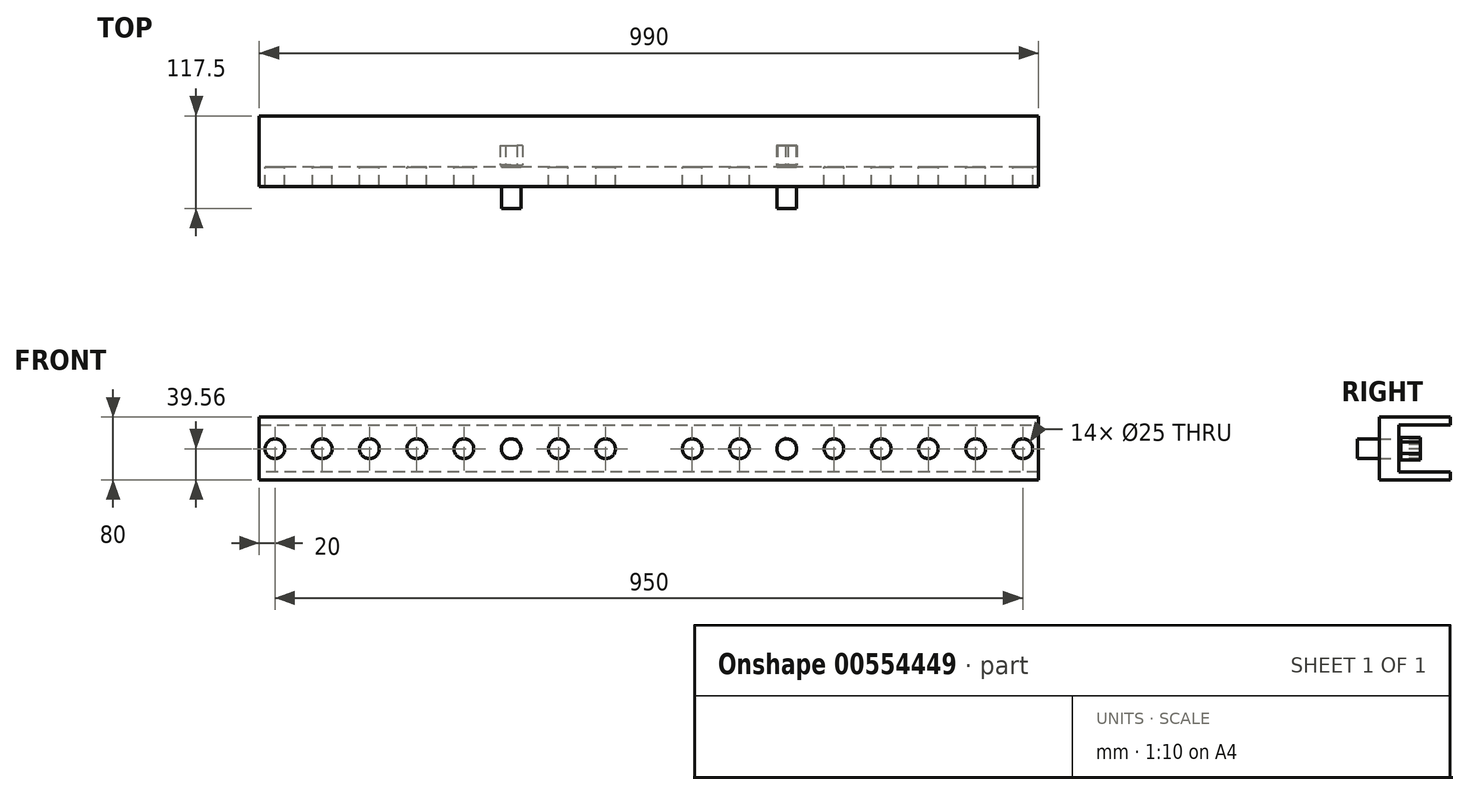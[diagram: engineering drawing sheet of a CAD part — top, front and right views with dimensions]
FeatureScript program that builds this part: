
annotation { "Feature Type Name" : "Feature", "Feature Type Description" : "" }
export const myFeature = defineFeature(function(context is Context, id is Id, definition is map)
    precondition{}
    {
        {
            var Q0;
            Q0=qCreatedBy(makeId("Front.planeOp"),FACE);
            var sketch = newSketch(context, id + "F0", { "sketchPlane" : qUnion([Q0])});
            skLineSegment(sketch, "E0.top", {"start": v(-325, -39.56) * mm, "end": v(325, -39.56) * mm});
            skLineSegment(sketch, "E0.left", {"start": v(-325, 40.44) * mm, "end": v(-325, -39.56) * mm});
            skLineSegment(sketch, "E0.right", {"start": v(325, 40.44) * mm, "end": v(325, -39.56) * mm});
            skLineSegment(sketch, "E1", {"start": v(-325, 40.44) * mm, "end": v(0, 40.44) * mm});
            skLineSegment(sketch, "E2", {"start": v(0, 40.44) * mm, "end": v(325, 40.44) * mm});
            skCircle(sketch, "E3", {"center": v(-295, 0) * mm, "radius": 12.5 * mm});
            skCircle(sketch, "E4", {"center": v(-235, 0) * mm, "radius": 12.5 * mm});
            skCircle(sketch, "E5", {"center": v(-175, 0) * mm, "radius": 12.5 * mm});
            skCircle(sketch, "E6", {"center": v(175, 0) * mm, "radius": 12.5 * mm});
            skCircle(sketch, "E7", {"center": v(235, 0) * mm, "radius": 12.5 * mm});
            skCircle(sketch, "E8", {"center": v(295, 0) * mm, "radius": 12.5 * mm});
            skLineSegment(sketch, "E9", {"start": v(325, 40.44) * mm, "end": v(495, 40.44) * mm});
            skLineSegment(sketch, "E10", {"start": v(-325, 40.44) * mm, "end": v(-495, 40.44) * mm});
            skLineSegment(sketch, "E11", {"start": v(-495, 40.44) * mm, "end": v(-495, -39.56) * mm});
            skLineSegment(sketch, "E12", {"start": v(-495, -39.56) * mm, "end": v(-325, -39.56) * mm});
            skLineSegment(sketch, "E13", {"start": v(495, 40.44) * mm, "end": v(495, -39.56) * mm});
            skLineSegment(sketch, "E14", {"start": v(495, -39.56) * mm, "end": v(325, -39.56) * mm});
            skCircle(sketch, "E15", {"center": v(355, 0) * mm, "radius": 12.5 * mm});
            skCircle(sketch, "E16", {"center": v(415, 0) * mm, "radius": 12.5 * mm});
            skCircle(sketch, "E17", {"center": v(475, 0) * mm, "radius": 12.5 * mm});
            skCircle(sketch, "E18", {"center": v(115, 0) * mm, "radius": 12.5 * mm});
            skCircle(sketch, "E19", {"center": v(55, 0) * mm, "radius": 12.5 * mm});
            skCircle(sketch, "E20", {"center": v(-55, 0) * mm, "radius": 12.5 * mm});
            skCircle(sketch, "E21", {"center": v(-115, 0) * mm, "radius": 12.5 * mm});
            skCircle(sketch, "E22", {"center": v(-355, 0) * mm, "radius": 12.5 * mm});
            skCircle(sketch, "E23", {"center": v(-415, 0) * mm, "radius": 12.5 * mm});
            skCircle(sketch, "E24", {"center": v(-475, 0) * mm, "radius": 12.5 * mm});
            skSolve(sketch);
        }
        {
            var Q0;
            Q0 = qSketchRegion(id + "F0", true);
            extrude(context, id + "F1", {"entities" : qUnion([Q0]), "depth" : 25 * mm, "offsetDistance" : 25 * mm});
        }
        {
            var Q0;
            {var subQ0=sQuery(id+"F0.wireOp",EDGE,"E8");var subQ1=sQuery(id+"F0.wireOp",EDGE,"E7");var subQ2=sQuery(id+"F0.wireOp",EDGE,"E6");var subQ3=sQuery(id+"F0.wireOp",EDGE,"E5");var subQ4=sQuery(id+"F0.wireOp",EDGE,"E4");var subQ5=sQuery(id+"F0.wireOp",EDGE,"E3");Q0=makeQuery(id+"FZENVl10s8qZQgk_7.boolean.opBoolean","MERGE",FACE,{"derivedFrom":[makeQuery(id+"Faq082uHJgfn2bv_0.opExtrude","CAP_FACE",FACE,{"disambiguationData":[OSD([subQ5])],"isStart":true}),makeQuery(id+"Faq082uHJgfn2bv_0.opExtrude","CAP_FACE",FACE,{"disambiguationData":[OSD([subQ4])],"isStart":true}),makeQuery(id+"Faq082uHJgfn2bv_0.opExtrude","CAP_FACE",FACE,{"disambiguationData":[OSD([subQ3])],"isStart":true}),makeQuery(id+"Faq082uHJgfn2bv_0.opExtrude","CAP_FACE",FACE,{"disambiguationData":[OSD([subQ2])],"isStart":true}),makeQuery(id+"Faq082uHJgfn2bv_0.opExtrude","CAP_FACE",FACE,{"disambiguationData":[OSD([subQ1])],"isStart":true}),makeQuery(id+"Faq082uHJgfn2bv_0.opExtrude","CAP_FACE",FACE,{"disambiguationData":[OSD([subQ0])],"isStart":true}),makeQuery(id+"F1.opExtrude","CAP_FACE",FACE,{"disambiguationData":[OSD([sQuery(id+"F0.wireOp",EDGE,"E0.top"),sQuery(id+"F0.wireOp",EDGE,"E1"),sQuery(id+"F0.wireOp",EDGE,"E2"),subQ5,subQ4,subQ3,subQ2,subQ1,subQ0,sQuery(id+"F0.wireOp",EDGE,"E9"),sQuery(id+"F0.wireOp",EDGE,"E10"),sQuery(id+"F0.wireOp",EDGE,"E11"),sQuery(id+"F0.wireOp",EDGE,"E12"),sQuery(id+"F0.wireOp",EDGE,"E13"),sQuery(id+"F0.wireOp",EDGE,"E14")])],"isStart":true})]});}
            var sketch = newSketch(context, id + "F2", { "sketchPlane" : qUnion([Q0])});
            skLineSegment(sketch, "E25", {"start": v(-495, 40.44) * mm, "end": v(495, 40.44) * mm});
            skLineSegment(sketch, "E26", {"start": v(495, 40.44) * mm, "end": v(496.19, 30.44) * mm});
            skLineSegment(sketch, "E27", {"start": v(496.19, 30.44) * mm, "end": v(-495, 30.44) * mm});
            skLineSegment(sketch, "E28", {"start": v(-495, 30.44) * mm, "end": v(-495, 40.44) * mm});
            skLineSegment(sketch, "E29", {"start": v(-495, -39.56) * mm, "end": v(-495, -29.56) * mm});
            skLineSegment(sketch, "E30", {"start": v(-495, -29.56) * mm, "end": v(495, -29.56) * mm});
            skLineSegment(sketch, "E31", {"start": v(495, -29.56) * mm, "end": v(495, -39.56) * mm});
            skLineSegment(sketch, "E32", {"start": v(495, -39.56) * mm, "end": v(-495, -39.56) * mm});
            skSolve(sketch);
        }
        {
            var Q0;
            {var subQ0=sQuery(id+"F2.wireOp",EDGE,"E25");Q0=makeQuery(id+"F2.imprint","IMPRINT",FACE,{"disambiguationData":[TD([[makeQuery(id+"F2.imprint","IMPRINT",EDGE,{"derivedFrom":subQ0}),-1.0]])]});}
            var Q1;
            Q1=makeQuery(id+"F2.imprint","IMPRINT",FACE,{"disambiguationData":[TD([[makeQuery(id+"F2.imprint","IMPRINT",EDGE,{"derivedFrom":sQuery(id+"F2.wireOp",EDGE,"E29")}),1.0]])]});
            extrude(context, id + "F3", {"entities" : qUnion([Q0, Q1]), "operationType" : NewBodyOperationType.ADD, "depth" : 65 * mm, "offsetDistance" : 25 * mm});
        }
        {
            var Q0;
            Q0=makeQuery(id+"F1.opExtrude","CAP_FACE",FACE,{"disambiguationData":[OSD([sQuery(id+"F0.wireOp",EDGE,"E0.top"),sQuery(id+"F0.wireOp",EDGE,"E1"),sQuery(id+"F0.wireOp",EDGE,"E2"),sQuery(id+"F0.wireOp",EDGE,"E3"),sQuery(id+"F0.wireOp",EDGE,"E4"),sQuery(id+"F0.wireOp",EDGE,"E5"),sQuery(id+"F0.wireOp",EDGE,"E6"),sQuery(id+"F0.wireOp",EDGE,"E7"),sQuery(id+"F0.wireOp",EDGE,"E8"),sQuery(id+"F0.wireOp",EDGE,"E9"),sQuery(id+"F0.wireOp",EDGE,"E10"),sQuery(id+"F0.wireOp",EDGE,"E11"),sQuery(id+"F0.wireOp",EDGE,"E12"),sQuery(id+"F0.wireOp",EDGE,"E13"),sQuery(id+"F0.wireOp",EDGE,"E14"),sQuery(id+"F0.wireOp",EDGE,"E15"),sQuery(id+"F0.wireOp",EDGE,"E16"),sQuery(id+"F0.wireOp",EDGE,"E17"),sQuery(id+"F0.wireOp",EDGE,"E18"),sQuery(id+"F0.wireOp",EDGE,"E19"),sQuery(id+"F0.wireOp",EDGE,"E20"),sQuery(id+"F0.wireOp",EDGE,"E21"),sQuery(id+"F0.wireOp",EDGE,"E22"),sQuery(id+"F0.wireOp",EDGE,"E23"),sQuery(id+"F0.wireOp",EDGE,"E24")])],"isStart":false});
            var sketch = newSketch(context, id + "F4", { "sketchPlane" : qUnion([Q0])});
            skCircle(sketch, "E33", {"center": v(175, 0) * mm, "radius": 12.5 * mm});
            skCircle(sketch, "E34", {"center": v(-175, 0) * mm, "radius": 12.5 * mm});
            skSolve(sketch);
        }
        {
            var Q0;
            Q0 = qSketchRegion(id + "F4", true);
            extrude(context, id + "F5", {"entities" : qUnion([Q0]), "operationType" : NewBodyOperationType.ADD, "endBound" : BoundingType.SYMMETRIC, "depth" : 55 * mm, "offsetDistance" : 25 * mm});
        }
        {
            var Q0;
            Q0=makeQuery(id+"F5.opExtrude","CAP_FACE",FACE,{"disambiguationData":[OSD([sQuery(id+"F4.wireOp",EDGE,"E33")])],"isStart":true});
            var sketch = newSketch(context, id + "F6", { "sketchPlane" : qUnion([Q0])});
            skCircle(sketch, "E35.cCircle", {"center": v(-175, 0) * mm, "radius": 12.5 * mm, "construction": true});
            skLineSegment(sketch, "E35.0", {"start": v(-163.44, -8.64) * mm, "end": v(-176.7, -14.33) * mm});
            skLineSegment(sketch, "E35.1", {"start": v(-176.7, -14.33) * mm, "end": v(-188.26, -5.7) * mm});
            skLineSegment(sketch, "E35.2", {"start": v(-188.26, -5.7) * mm, "end": v(-186.56, 8.64) * mm});
            skLineSegment(sketch, "E35.3", {"start": v(-186.56, 8.64) * mm, "end": v(-173.3, 14.33) * mm});
            skLineSegment(sketch, "E35.4", {"start": v(-173.3, 14.33) * mm, "end": v(-161.74, 5.7) * mm});
            skLineSegment(sketch, "E35.5", {"start": v(-161.74, 5.7) * mm, "end": v(-163.44, -8.64) * mm});
            skPoint(sketch, "E35.0.midPoint", {"position": v(-170.07, -11.49) * mm});
            skSolve(sketch);
        }
        {
            var Q0;
            Q0=makeQuery(id+"F5.opExtrude","CAP_FACE",FACE,{"disambiguationData":[OSD([sQuery(id+"F4.wireOp",EDGE,"E34")])],"isStart":true});
            var sketch = newSketch(context, id + "F7", { "sketchPlane" : qUnion([Q0])});
            skCircle(sketch, "E36.cCircle", {"center": v(175, 0) * mm, "radius": 12.5 * mm, "construction": true});
            skLineSegment(sketch, "E36.0", {"start": v(182.22, -12.5) * mm, "end": v(167.78, -12.5) * mm});
            skLineSegment(sketch, "E36.1", {"start": v(167.78, -12.5) * mm, "end": v(160.57, 0) * mm});
            skLineSegment(sketch, "E36.2", {"start": v(160.57, 0) * mm, "end": v(167.78, 12.5) * mm});
            skLineSegment(sketch, "E36.3", {"start": v(167.78, 12.5) * mm, "end": v(182.22, 12.5) * mm});
            skLineSegment(sketch, "E36.4", {"start": v(182.22, 12.5) * mm, "end": v(189.43, 0) * mm});
            skLineSegment(sketch, "E36.5", {"start": v(189.43, 0) * mm, "end": v(182.22, -12.5) * mm});
            skPoint(sketch, "E36.0.midPoint", {"position": v(175, -12.5) * mm});
            skSolve(sketch);
        }
        {
            var Q0;
            {var subQ0=sQuery(id+"F6.wireOp",EDGE,"E35.4");var subQ1=sQuery(id+"F6.wireOp",EDGE,"E35.3");var subQ2=makeQuery(id+"F6.imprint","INTERSECT",VERTEX,{"derivedFrom":[subQ1,subQ0]});Q0=makeQuery(id+"F6.imprint","IMPRINT",FACE,{"disambiguationData":[TD([[makeQuery(id+"F6.imprint","IMPRINT",EDGE,{"disambiguationData":[TD([[subQ2,1.0]])],"derivedFrom":subQ1}),-1.0]])]});}
            var Q1;
            {var subQ0=sQuery(id+"F6.wireOp",EDGE,"E35.5");var subQ1=sQuery(id+"F6.wireOp",EDGE,"E35.4");var subQ2=makeQuery(id+"F6.imprint","INTERSECT",VERTEX,{"derivedFrom":[subQ1,subQ0]});Q1=makeQuery(id+"F6.imprint","IMPRINT",FACE,{"disambiguationData":[TD([[makeQuery(id+"F6.imprint","IMPRINT",EDGE,{"disambiguationData":[TD([[subQ2,1.0]])],"derivedFrom":subQ1}),-1.0]])]});}
            var Q2;
            {var subQ0=sQuery(id+"F6.wireOp",EDGE,"E35.5");var subQ1=sQuery(id+"F6.wireOp",EDGE,"E35.0");var subQ2=makeQuery(id+"F6.imprint","INTERSECT",VERTEX,{"derivedFrom":[subQ1,subQ0]});Q2=makeQuery(id+"F6.imprint","IMPRINT",FACE,{"disambiguationData":[TD([[makeQuery(id+"F6.imprint","IMPRINT",EDGE,{"disambiguationData":[TD([[subQ2,-1.0]])],"derivedFrom":subQ1}),-1.0]])]});}
            var Q3;
            {var subQ0=sQuery(id+"F6.wireOp",EDGE,"E35.1");var subQ1=sQuery(id+"F6.wireOp",EDGE,"E35.0");var subQ2=makeQuery(id+"F6.imprint","INTERSECT",VERTEX,{"derivedFrom":[subQ1,subQ0]});Q3=makeQuery(id+"F6.imprint","IMPRINT",FACE,{"disambiguationData":[TD([[makeQuery(id+"F6.imprint","IMPRINT",EDGE,{"disambiguationData":[TD([[subQ2,1.0]])],"derivedFrom":subQ1}),-1.0]])]});}
            var Q4;
            {var subQ0=sQuery(id+"F6.wireOp",EDGE,"E35.2");var subQ1=sQuery(id+"F6.wireOp",EDGE,"E35.1");var subQ2=makeQuery(id+"F6.imprint","INTERSECT",VERTEX,{"derivedFrom":[subQ1,subQ0]});Q4=makeQuery(id+"F6.imprint","IMPRINT",FACE,{"disambiguationData":[TD([[makeQuery(id+"F6.imprint","IMPRINT",EDGE,{"disambiguationData":[TD([[subQ2,1.0]])],"derivedFrom":subQ1}),-1.0]])]});}
            var Q5;
            {var subQ0=sQuery(id+"F6.wireOp",EDGE,"E35.3");var subQ1=sQuery(id+"F6.wireOp",EDGE,"E35.2");var subQ2=makeQuery(id+"F6.imprint","INTERSECT",VERTEX,{"derivedFrom":[subQ1,subQ0]});Q5=makeQuery(id+"F6.imprint","IMPRINT",FACE,{"disambiguationData":[TD([[makeQuery(id+"F6.imprint","IMPRINT",EDGE,{"disambiguationData":[TD([[subQ2,1.0]])],"derivedFrom":subQ1}),-1.0]])]});}
            var Q6;
            {var subQ0=makeQuery(id+"F5.opExtrude","CAP_EDGE",EDGE,{"disambiguationData":[OSD([sQuery(id+"F4.wireOp",EDGE,"E33")])],"isStart":true});var subQ4=makeQuery(id+"F6.imprint","INTERSECT",VERTEX,{"derivedFrom":[subQ0,sQuery(id+"F6.wireOp",EDGE,"E35.0")]});Q6=makeQuery(id+"F6.imprint","IMPRINT",FACE,{"disambiguationData":[TD([[makeQuery(id+"F6.imprint","IMPRINT",EDGE,{"disambiguationData":[TD([[subQ4,-1.0]])],"derivedFrom":subQ0}),-1.0]])]});}
            extrude(context, id + "F8", {"entities" : qUnion([Q0, Q1, Q2, Q3, Q4, Q5, Q6]), "operationType" : NewBodyOperationType.ADD, "depth" : 25 * mm, "offsetDistance" : 25 * mm});
        }
        {
            var Q0;
            {var subQ0=sQuery(id+"F7.wireOp",EDGE,"E36.2");var subQ1=sQuery(id+"F7.wireOp",EDGE,"E36.1");var subQ2=makeQuery(id+"F7.imprint","INTERSECT",VERTEX,{"derivedFrom":[subQ1,subQ0]});Q0=makeQuery(id+"F7.imprint","IMPRINT",FACE,{"disambiguationData":[TD([[makeQuery(id+"F7.imprint","IMPRINT",EDGE,{"disambiguationData":[TD([[subQ2,1.0]])],"derivedFrom":subQ1}),-1.0]])]});}
            var Q1;
            {var subQ0=sQuery(id+"F7.wireOp",EDGE,"E36.3");var subQ1=sQuery(id+"F7.wireOp",EDGE,"E36.2");var subQ2=makeQuery(id+"F7.imprint","INTERSECT",VERTEX,{"derivedFrom":[subQ1,subQ0]});Q1=makeQuery(id+"F7.imprint","IMPRINT",FACE,{"disambiguationData":[TD([[makeQuery(id+"F7.imprint","IMPRINT",EDGE,{"disambiguationData":[TD([[subQ2,1.0]])],"derivedFrom":subQ1}),-1.0]])]});}
            var Q2;
            {var subQ0=sQuery(id+"F7.wireOp",EDGE,"E36.4");var subQ1=sQuery(id+"F7.wireOp",EDGE,"E36.3");var subQ2=makeQuery(id+"F7.imprint","INTERSECT",VERTEX,{"derivedFrom":[subQ1,subQ0]});Q2=makeQuery(id+"F7.imprint","IMPRINT",FACE,{"disambiguationData":[TD([[makeQuery(id+"F7.imprint","IMPRINT",EDGE,{"disambiguationData":[TD([[subQ2,1.0]])],"derivedFrom":subQ1}),-1.0]])]});}
            var Q3;
            {var subQ0=sQuery(id+"F7.wireOp",EDGE,"E36.5");var subQ1=sQuery(id+"F7.wireOp",EDGE,"E36.4");var subQ2=makeQuery(id+"F7.imprint","INTERSECT",VERTEX,{"derivedFrom":[subQ1,subQ0]});Q3=makeQuery(id+"F7.imprint","IMPRINT",FACE,{"disambiguationData":[TD([[makeQuery(id+"F7.imprint","IMPRINT",EDGE,{"disambiguationData":[TD([[subQ2,1.0]])],"derivedFrom":subQ1}),-1.0]])]});}
            var Q4;
            {var subQ0=sQuery(id+"F7.wireOp",EDGE,"E36.5");var subQ1=sQuery(id+"F7.wireOp",EDGE,"E36.0");var subQ2=makeQuery(id+"F7.imprint","INTERSECT",VERTEX,{"derivedFrom":[subQ1,subQ0]});Q4=makeQuery(id+"F7.imprint","IMPRINT",FACE,{"disambiguationData":[TD([[makeQuery(id+"F7.imprint","IMPRINT",EDGE,{"disambiguationData":[TD([[subQ2,-1.0]])],"derivedFrom":subQ1}),-1.0]])]});}
            var Q5;
            {var subQ0=sQuery(id+"F7.wireOp",EDGE,"E36.1");var subQ1=sQuery(id+"F7.wireOp",EDGE,"E36.0");var subQ2=makeQuery(id+"F7.imprint","INTERSECT",VERTEX,{"derivedFrom":[subQ1,subQ0]});Q5=makeQuery(id+"F7.imprint","IMPRINT",FACE,{"disambiguationData":[TD([[makeQuery(id+"F7.imprint","IMPRINT",EDGE,{"disambiguationData":[TD([[subQ2,1.0]])],"derivedFrom":subQ1}),-1.0]])]});}
            var Q6;
            {var subQ0=makeQuery(id+"F5.opExtrude","CAP_EDGE",EDGE,{"disambiguationData":[OSD([sQuery(id+"F4.wireOp",EDGE,"E34")])],"isStart":true});var subQ4=makeQuery(id+"F7.imprint","INTERSECT",VERTEX,{"derivedFrom":[subQ0,sQuery(id+"F7.wireOp",EDGE,"E36.0")]});Q6=makeQuery(id+"F7.imprint","IMPRINT",FACE,{"disambiguationData":[TD([[makeQuery(id+"F7.imprint","IMPRINT",EDGE,{"disambiguationData":[TD([[subQ4,-1.0]])],"derivedFrom":subQ0}),-1.0]])]});}
            extrude(context, id + "F9", {"entities" : qUnion([Q0, Q1, Q2, Q3, Q4, Q5, Q6]), "operationType" : NewBodyOperationType.ADD, "depth" : 25 * mm, "offsetDistance" : 25 * mm});
        }
    });
